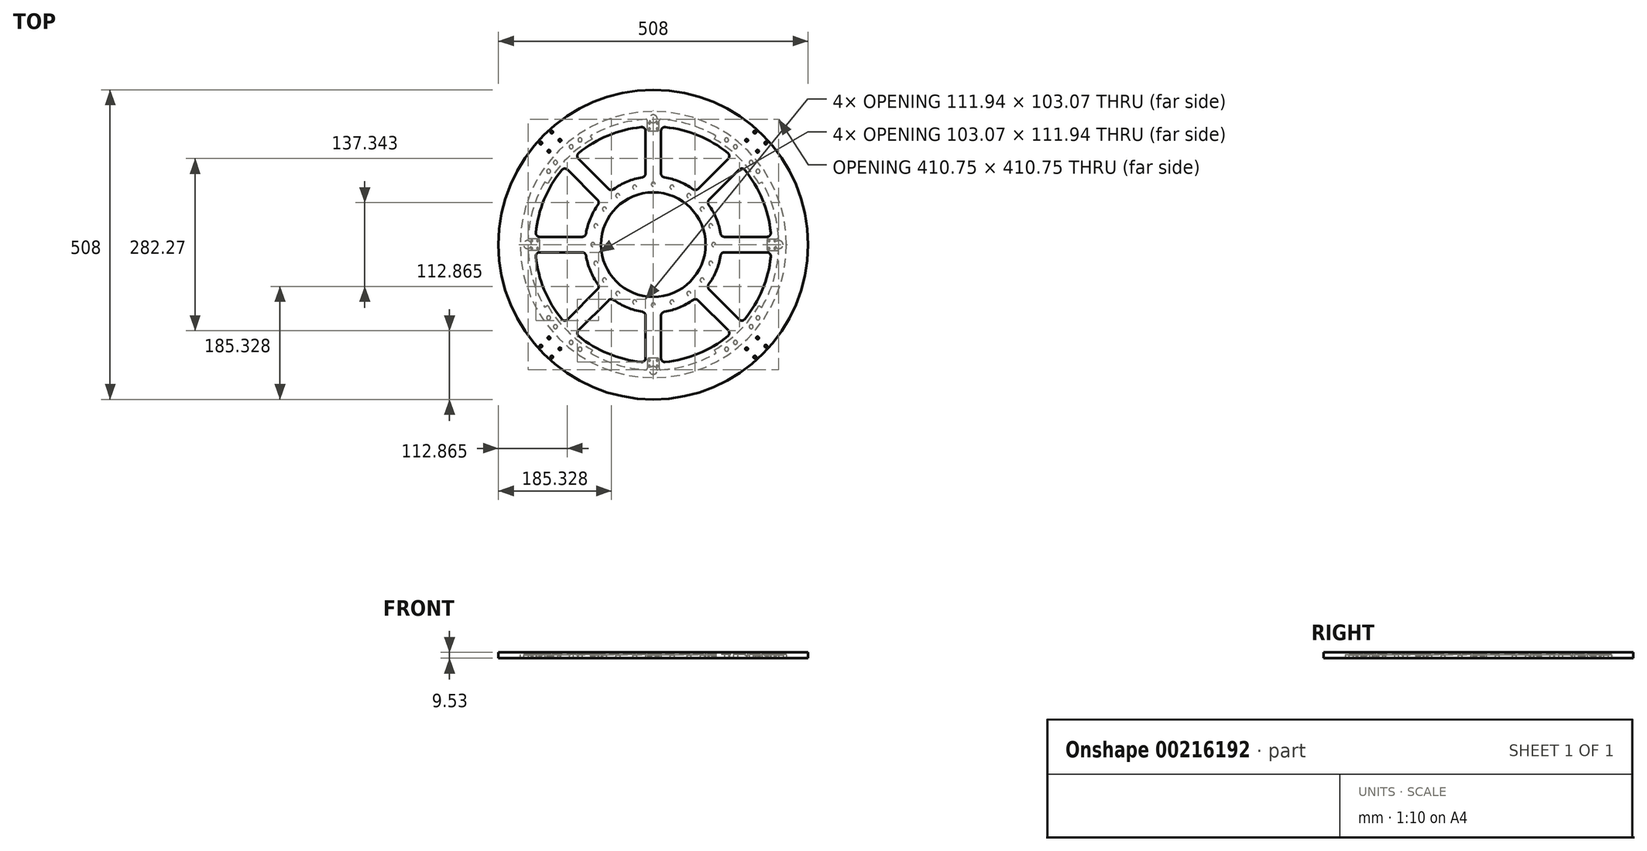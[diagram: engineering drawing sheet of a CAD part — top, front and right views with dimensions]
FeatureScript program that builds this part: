
annotation { "Feature Type Name" : "Feature", "Feature Type Description" : "" }
export const myFeature = defineFeature(function(context is Context, id is Id, definition is map)
    precondition{}
    {
        {
            var Q0;
            Q0=qCreatedBy(makeId("Top.planeOp"),FACE);
            var sketch = newSketch(context, id + "F0", { "sketchPlane" : qUnion([Q0])});
            skCircle(sketch, "E0", {"center": v(0, 0) * mm, "radius": 218.44 * mm});
            skArc(sketch, "E1", {"start": v(205.38, 12.22) * mm, "mid": v(197.06, 59.13) * mm, "end": v(178.18, 102.87) * mm});
            skLineSegment(sketch, "E2", {"start": v(0, 0) * mm, "end": v(218.44, 0) * mm});
            skLineSegment(sketch, "E3", {"start": v(199.4, 6.35) * mm, "end": v(189.87, 6.35) * mm});
            skLineSegment(sketch, "E4.MirrorCS", {"start": v(199.4, -6.35) * mm, "end": v(189.87, -6.35) * mm});
            skLineSegment(sketch, "E5.bottom", {"start": v(188.91, 9.52) * mm, "end": v(202.88, 9.52) * mm});
            skLineSegment(sketch, "E5.top", {"start": v(188.91, -9.52) * mm, "end": v(202.88, -9.52) * mm});
            skLineSegment(sketch, "E5.left", {"start": v(186.37, 6.98) * mm, "end": v(186.37, -6.98) * mm});
            skPoint(sketch, "E5.middle", {"position": v(194.63, 0) * mm});
            skLineSegment(sketch, "E6", {"start": v(202.84, 9.52) * mm, "end": v(202.88, 9.52) * mm});
            skPoint(sketch, "E7.orphan", {"position": v(199.4, -6.35) * mm});
            skPoint(sketch, "E8.orphan", {"position": v(205.74, 12.7) * mm});
            skPoint(sketch, "E9.start.orphan", {"position": v(205.74, 0) * mm});
            skPoint(sketch, "E10.visualSharp", {"position": v(205.52, 9.52) * mm});
            skArc(sketch, "E10.filletArc", {"start": v(202.84, 9.52) * mm, "mid": v(204.7, 10.32) * mm, "end": v(205.38, 12.22) * mm});
            skPoint(sketch, "E11.orphan", {"position": v(205.74, -12.7) * mm});
            skPoint(sketch, "E12.MirrorCS.end.orphan", {"position": v(205.74, -6.35) * mm});
            skLineSegment(sketch, "E13", {"start": v(202.84, -9.52) * mm, "end": v(202.88, -9.52) * mm});
            skArc(sketch, "E14.filletArc", {"start": v(205.38, -12.22) * mm, "mid": v(204.7, -10.32) * mm, "end": v(202.84, -9.52) * mm});
            skPoint(sketch, "E15.visualSharp", {"position": v(186.37, 9.52) * mm});
            skArc(sketch, "E15.filletArc", {"start": v(188.91, 9.52) * mm, "mid": v(187.12, 8.78) * mm, "end": v(186.37, 6.98) * mm});
            skPoint(sketch, "E16.visualSharp", {"position": v(186.37, -9.53) * mm});
            skArc(sketch, "E16.filletArc", {"start": v(186.37, -6.98) * mm, "mid": v(187.12, -8.78) * mm, "end": v(188.91, -9.52) * mm});
            skPoint(sketch, "E17.start.orphan", {"position": v(205.74, 6.35) * mm});
            skPoint(sketch, "E18.1.0", {"position": v(-6.35, 205.74) * mm});
            skPoint(sketch, "E18.1.1", {"position": v(-12.7, 205.74) * mm});
            skPoint(sketch, "E18.1.2", {"position": v(6.35, 205.74) * mm});
            skPoint(sketch, "E18.1.3", {"position": v(6.35, 199.4) * mm});
            skPoint(sketch, "E18.1.4", {"position": v(12.7, 205.74) * mm});
            skPoint(sketch, "E18.1.5", {"position": v(9.53, 186.37) * mm});
            skPoint(sketch, "E18.1.6", {"position": v(-9.52, 186.37) * mm});
            skPoint(sketch, "E18.1.7", {"position": v(0, 194.63) * mm});
            skPoint(sketch, "E18.1.8", {"position": v(6.35, 205.74) * mm});
            skPoint(sketch, "E18.1.9", {"position": v(-9.52, 205.52) * mm});
            skPoint(sketch, "E18.1.10", {"position": v(0, 205.74) * mm});
            skLineSegment(sketch, "E18.1.11", {"start": v(-6.98, 186.37) * mm, "end": v(6.99, 186.37) * mm});
            skPoint(sketch, "E18.1.12", {"position": v(0, 205.74) * mm});
            skLineSegment(sketch, "E18.1.13", {"start": v(9.53, 188.91) * mm, "end": v(9.53, 202.88) * mm});
            skLineSegment(sketch, "E18.1.14", {"start": v(-9.52, 188.91) * mm, "end": v(-9.52, 202.88) * mm});
            skLineSegment(sketch, "E18.1.15", {"start": v(6.35, 199.4) * mm, "end": v(6.35, 189.87) * mm});
            skLineSegment(sketch, "E18.1.16", {"start": v(-6.35, 199.4) * mm, "end": v(-6.35, 189.87) * mm});
            skArc(sketch, "E18.1.17", {"start": v(-9.52, 188.91) * mm, "mid": v(-8.78, 187.12) * mm, "end": v(-6.98, 186.37) * mm});
            skPoint(sketch, "E18.1.18", {"position": v(0, 205.74) * mm});
            skArc(sketch, "E18.1.19", {"start": v(6.99, 186.37) * mm, "mid": v(8.78, 187.12) * mm, "end": v(9.53, 188.91) * mm});
            skArc(sketch, "E18.1.20", {"start": v(12.22, 205.38) * mm, "mid": v(10.32, 204.7) * mm, "end": v(9.53, 202.84) * mm});
            skArc(sketch, "E18.1.21", {"start": v(-9.52, 202.84) * mm, "mid": v(-10.32, 204.7) * mm, "end": v(-12.22, 205.38) * mm});
            skLineSegment(sketch, "E18.1.22", {"start": v(-9.52, 202.84) * mm, "end": v(-9.52, 202.88) * mm});
            skLineSegment(sketch, "E18.1.23", {"start": v(9.53, 202.84) * mm, "end": v(9.53, 202.88) * mm});
            skPoint(sketch, "E18.2.0", {"position": v(-205.74, -6.35) * mm});
            skPoint(sketch, "E18.2.1", {"position": v(-205.74, -12.7) * mm});
            skPoint(sketch, "E18.2.2", {"position": v(-205.74, 6.35) * mm});
            skPoint(sketch, "E18.2.3", {"position": v(-199.4, 6.35) * mm});
            skPoint(sketch, "E18.2.4", {"position": v(-205.74, 12.7) * mm});
            skPoint(sketch, "E18.2.5", {"position": v(-186.37, 9.53) * mm});
            skPoint(sketch, "E18.2.6", {"position": v(-186.37, -9.52) * mm});
            skPoint(sketch, "E18.2.7", {"position": v(-194.63, 0) * mm});
            skPoint(sketch, "E18.2.8", {"position": v(-205.74, 6.35) * mm});
            skPoint(sketch, "E18.2.9", {"position": v(-205.52, -9.52) * mm});
            skPoint(sketch, "E18.2.10", {"position": v(-205.74, 0) * mm});
            skLineSegment(sketch, "E18.2.11", {"start": v(-186.37, -6.98) * mm, "end": v(-186.37, 6.99) * mm});
            skPoint(sketch, "E18.2.12", {"position": v(-205.74, 0) * mm});
            skLineSegment(sketch, "E18.2.13", {"start": v(-188.91, 9.53) * mm, "end": v(-202.88, 9.53) * mm});
            skLineSegment(sketch, "E18.2.14", {"start": v(-188.91, -9.52) * mm, "end": v(-202.88, -9.52) * mm});
            skLineSegment(sketch, "E18.2.15", {"start": v(-199.4, 6.35) * mm, "end": v(-189.87, 6.35) * mm});
            skLineSegment(sketch, "E18.2.16", {"start": v(-199.4, -6.35) * mm, "end": v(-189.87, -6.35) * mm});
            skArc(sketch, "E18.2.17", {"start": v(-188.91, -9.52) * mm, "mid": v(-187.12, -8.78) * mm, "end": v(-186.37, -6.98) * mm});
            skPoint(sketch, "E18.2.18", {"position": v(-205.74, 0) * mm});
            skArc(sketch, "E18.2.19", {"start": v(-186.37, 6.99) * mm, "mid": v(-187.12, 8.78) * mm, "end": v(-188.91, 9.53) * mm});
            skArc(sketch, "E18.2.20", {"start": v(-205.38, 12.22) * mm, "mid": v(-204.7, 10.32) * mm, "end": v(-202.84, 9.53) * mm});
            skArc(sketch, "E18.2.21", {"start": v(-202.84, -9.52) * mm, "mid": v(-204.7, -10.32) * mm, "end": v(-205.38, -12.22) * mm});
            skLineSegment(sketch, "E18.2.22", {"start": v(-202.84, -9.52) * mm, "end": v(-202.88, -9.52) * mm});
            skLineSegment(sketch, "E18.2.23", {"start": v(-202.84, 9.53) * mm, "end": v(-202.88, 9.53) * mm});
            skPoint(sketch, "E18.3.0", {"position": v(6.35, -205.74) * mm});
            skPoint(sketch, "E18.3.1", {"position": v(12.7, -205.74) * mm});
            skPoint(sketch, "E18.3.2", {"position": v(-6.35, -205.74) * mm});
            skPoint(sketch, "E18.3.3", {"position": v(-6.35, -199.4) * mm});
            skPoint(sketch, "E18.3.4", {"position": v(-12.7, -205.74) * mm});
            skPoint(sketch, "E18.3.5", {"position": v(-9.53, -186.37) * mm});
            skPoint(sketch, "E18.3.6", {"position": v(9.52, -186.37) * mm});
            skPoint(sketch, "E18.3.7", {"position": v(0, -194.63) * mm});
            skPoint(sketch, "E18.3.8", {"position": v(-6.35, -205.74) * mm});
            skPoint(sketch, "E18.3.9", {"position": v(9.52, -205.52) * mm});
            skPoint(sketch, "E18.3.10", {"position": v(0, -205.74) * mm});
            skLineSegment(sketch, "E18.3.11", {"start": v(6.98, -186.37) * mm, "end": v(-6.99, -186.37) * mm});
            skPoint(sketch, "E18.3.12", {"position": v(0, -205.74) * mm});
            skLineSegment(sketch, "E18.3.13", {"start": v(-9.53, -188.91) * mm, "end": v(-9.53, -202.88) * mm});
            skLineSegment(sketch, "E18.3.14", {"start": v(9.52, -188.91) * mm, "end": v(9.52, -202.88) * mm});
            skLineSegment(sketch, "E18.3.15", {"start": v(-6.35, -199.4) * mm, "end": v(-6.35, -189.87) * mm});
            skLineSegment(sketch, "E18.3.16", {"start": v(6.35, -199.4) * mm, "end": v(6.35, -189.87) * mm});
            skArc(sketch, "E18.3.17", {"start": v(9.52, -188.91) * mm, "mid": v(8.78, -187.12) * mm, "end": v(6.98, -186.37) * mm});
            skPoint(sketch, "E18.3.18", {"position": v(0, -205.74) * mm});
            skArc(sketch, "E18.3.19", {"start": v(-6.99, -186.37) * mm, "mid": v(-8.78, -187.12) * mm, "end": v(-9.53, -188.91) * mm});
            skArc(sketch, "E18.3.20", {"start": v(-12.22, -205.38) * mm, "mid": v(-10.32, -204.7) * mm, "end": v(-9.53, -202.84) * mm});
            skArc(sketch, "E18.3.21", {"start": v(9.52, -202.84) * mm, "mid": v(10.32, -204.7) * mm, "end": v(12.22, -205.38) * mm});
            skLineSegment(sketch, "E18.3.22", {"start": v(9.53, -202.84) * mm, "end": v(9.53, -202.88) * mm});
            skLineSegment(sketch, "E18.3.23", {"start": v(-9.53, -202.84) * mm, "end": v(-9.53, -202.88) * mm});
            skArc(sketch, "E19.trimOffspring", {"start": v(-12.22, 205.38) * mm, "mid": v(-59.13, 197.06) * mm, "end": v(-102.87, 178.18) * mm});
            skArc(sketch, "E20.trimOffspring", {"start": v(-205.38, -12.22) * mm, "mid": v(-197.06, -59.13) * mm, "end": v(-178.18, -102.87) * mm});
            skArc(sketch, "E21.trimOffspring", {"start": v(12.22, -205.38) * mm, "mid": v(59.13, -197.06) * mm, "end": v(102.87, -178.18) * mm});
            skLineSegment(sketch, "E22", {"start": v(0, 0) * mm, "end": v(154.46, 154.46) * mm});
            skLineSegment(sketch, "E23", {"start": v(173.23, 100.01) * mm, "end": v(178.18, 102.87) * mm});
            skLineSegment(sketch, "E24.MirrorCS", {"start": v(100.01, 173.23) * mm, "end": v(102.87, 178.18) * mm});
            skArc(sketch, "E25.trimOffspring", {"start": v(173.23, 100.01) * mm, "mid": v(141.44, 141.44) * mm, "end": v(100.01, 173.23) * mm});
            skPoint(sketch, "E26.orphan", {"position": v(109.22, 189.17) * mm});
            skPoint(sketch, "E27.orphan", {"position": v(189.17, 109.22) * mm});
            skArc(sketch, "E28.1.0", {"start": v(-100.01, 173.23) * mm, "mid": v(-141.44, 141.44) * mm, "end": v(-173.23, 100.01) * mm});
            skLineSegment(sketch, "E28.1.1", {"start": v(-173.23, 100.01) * mm, "end": v(-178.18, 102.87) * mm});
            skLineSegment(sketch, "E28.1.2", {"start": v(-100.01, 173.23) * mm, "end": v(-102.87, 178.18) * mm});
            skArc(sketch, "E28.2.0", {"start": v(-173.23, -100.01) * mm, "mid": v(-141.44, -141.44) * mm, "end": v(-100.01, -173.23) * mm});
            skLineSegment(sketch, "E28.2.1", {"start": v(-100.01, -173.23) * mm, "end": v(-102.87, -178.18) * mm});
            skLineSegment(sketch, "E28.2.2", {"start": v(-173.23, -100.01) * mm, "end": v(-178.18, -102.87) * mm});
            skArc(sketch, "E28.3.0", {"start": v(100.01, -173.23) * mm, "mid": v(141.44, -141.44) * mm, "end": v(173.23, -100.01) * mm});
            skLineSegment(sketch, "E28.3.1", {"start": v(173.23, -100.01) * mm, "end": v(178.18, -102.87) * mm});
            skLineSegment(sketch, "E28.3.2", {"start": v(100.01, -173.23) * mm, "end": v(102.87, -178.18) * mm});
            skArc(sketch, "E29.trimOffspring", {"start": v(-178.18, 102.87) * mm, "mid": v(-197.06, 59.13) * mm, "end": v(-205.38, 12.22) * mm});
            skArc(sketch, "E30.trimOffspring", {"start": v(-102.87, -178.18) * mm, "mid": v(-59.13, -197.06) * mm, "end": v(-12.22, -205.38) * mm});
            skArc(sketch, "E31.trimOffspring", {"start": v(178.18, -102.87) * mm, "mid": v(197.06, -59.13) * mm, "end": v(205.38, -12.22) * mm});
            skArc(sketch, "E32.trimOffspring", {"start": v(102.87, 178.18) * mm, "mid": v(59.13, 197.06) * mm, "end": v(12.22, 205.38) * mm});
            skArc(sketch, "E33", {"start": v(209.55, 0) * mm, "mid": v(185.87, 96.76) * mm, "end": v(120.2, 171.65) * mm});
            skLineSegment(sketch, "E34", {"start": v(128.57, 153.23) * mm, "end": v(134.7, 160.52) * mm});
            skLineSegment(sketch, "E35", {"start": v(114.73, 163.85) * mm, "end": v(120.2, 171.65) * mm});
            skLineSegment(sketch, "E36.MirrorCS", {"start": v(153.23, 128.57) * mm, "end": v(160.52, 134.7) * mm});
            skLineSegment(sketch, "E37.MirrorCS", {"start": v(163.85, 114.73) * mm, "end": v(171.65, 120.2) * mm});
            skPoint(sketch, "E38.orphan", {"position": v(125.3, 178.94) * mm});
            skPoint(sketch, "E39.orphan", {"position": v(140.41, 167.33) * mm});
            skPoint(sketch, "E40.orphan", {"position": v(167.33, 140.41) * mm});
            skPoint(sketch, "E41.orphan", {"position": v(178.94, 125.3) * mm});
            skLineSegment(sketch, "E42.1.0", {"start": v(-163.85, 114.73) * mm, "end": v(-171.65, 120.2) * mm});
            skLineSegment(sketch, "E42.1.1", {"start": v(-153.23, 128.57) * mm, "end": v(-160.52, 134.7) * mm});
            skLineSegment(sketch, "E42.1.2", {"start": v(-128.57, 153.23) * mm, "end": v(-134.7, 160.52) * mm});
            skLineSegment(sketch, "E42.1.3", {"start": v(-114.73, 163.85) * mm, "end": v(-120.2, 171.65) * mm});
            skLineSegment(sketch, "E42.2.0", {"start": v(-114.73, -163.85) * mm, "end": v(-120.2, -171.65) * mm});
            skLineSegment(sketch, "E42.2.1", {"start": v(-128.57, -153.23) * mm, "end": v(-134.7, -160.52) * mm});
            skLineSegment(sketch, "E42.2.2", {"start": v(-153.23, -128.57) * mm, "end": v(-160.52, -134.7) * mm});
            skLineSegment(sketch, "E42.2.3", {"start": v(-163.85, -114.73) * mm, "end": v(-171.65, -120.2) * mm});
            skLineSegment(sketch, "E42.3.0", {"start": v(163.85, -114.73) * mm, "end": v(171.65, -120.2) * mm});
            skLineSegment(sketch, "E42.3.1", {"start": v(153.23, -128.57) * mm, "end": v(160.52, -134.7) * mm});
            skLineSegment(sketch, "E42.3.2", {"start": v(128.57, -153.23) * mm, "end": v(134.7, -160.52) * mm});
            skLineSegment(sketch, "E42.3.3", {"start": v(114.73, -163.85) * mm, "end": v(120.2, -171.65) * mm});
            skLineSegment(sketch, "E43", {"start": v(205.74, 0) * mm, "end": v(205.74, -4.72) * mm});
            skLineSegment(sketch, "E44", {"start": v(199.4, -6.35) * mm, "end": v(199.4, 0) * mm});
            skSolve(sketch);
        }
        {
            var Q0;
            Q0 = qSketchRegion(id + "F0", true);
            var Q1;
            Q1=makeQuery(id+"F0.imprint","IMPRINT",FACE,{"disambiguationData":[TD([[makeQuery(id+"F0.imprint","IMPRINT",EDGE,{"derivedFrom":sQuery(id+"F0.wireOp",EDGE,"E1")}),-1.0]])]});
            var Q2;
            {var subQ0=sQuery(id+"F0.wireOp",EDGE,"E36.MirrorCS");Q2=makeQuery(id+"F0.imprint","IMPRINT",FACE,{"disambiguationData":[TD([[makeQuery(id+"F0.imprint","IMPRINT",EDGE,{"derivedFrom":subQ0}),-1.0]])]});}
            var Q3;
            {var subQ5=sQuery(id+"F0.wireOp",EDGE,"E36.MirrorCS");Q3=makeQuery(id+"F0.imprint","IMPRINT",FACE,{"disambiguationData":[TD([[makeQuery(id+"F0.imprint","IMPRINT",EDGE,{"derivedFrom":subQ5}),1.0]])]});}
            var Q4;
            {var subQ5=sQuery(id+"F0.wireOp",EDGE,"E34");Q4=makeQuery(id+"F0.imprint","IMPRINT",FACE,{"disambiguationData":[TD([[makeQuery(id+"F0.imprint","IMPRINT",EDGE,{"derivedFrom":subQ5}),-1.0]])]});}
            var Q5;
            {var subQ0=sQuery(id+"F0.wireOp",EDGE,"E34");Q5=makeQuery(id+"F0.imprint","IMPRINT",FACE,{"disambiguationData":[TD([[makeQuery(id+"F0.imprint","IMPRINT",EDGE,{"derivedFrom":subQ0}),1.0]])]});}
            extrude(context, id + "F1", {"entities" : qUnion([Q0, Q1, Q2, Q3, Q4, Q5]), "depth" : 6.1 * mm});
        }
        {
            var Q0;
            Q0=sQuery(id+"F0.wireOp",VERTEX,"E42.1.0.end");
            var Q1;
            Q1=sQuery(id+"F0.wireOp",VERTEX,"E42.1.1.end");
            var Q2;
            Q2=sQuery(id+"F0.wireOp",VERTEX,"E42.1.2.end");
            var Q3;
            Q3=sQuery(id+"F0.wireOp",VERTEX,"E42.1.3.end");
            var Q4;
            Q4=sQuery(id+"F0.wireOp",VERTEX,"E35.end");
            var Q5;
            Q5=sQuery(id+"F0.wireOp",VERTEX,"E34.end");
            var Q6;
            Q6=sQuery(id+"F0.wireOp",VERTEX,"E36.MirrorCS.end");
            var Q7;
            Q7=sQuery(id+"F0.wireOp",VERTEX,"E37.MirrorCS.end");
            var Q8;
            Q8=sQuery(id+"F0.wireOp",VERTEX,"E42.3.0.end");
            var Q9;
            Q9=sQuery(id+"F0.wireOp",VERTEX,"E42.3.1.end");
            var Q10;
            Q10=sQuery(id+"F0.wireOp",VERTEX,"E42.3.2.end");
            var Q11;
            Q11=sQuery(id+"F0.wireOp",VERTEX,"E42.3.3.end");
            var Q12;
            Q12=sQuery(id+"F0.wireOp",VERTEX,"E42.2.0.end");
            var Q13;
            Q13=sQuery(id+"F0.wireOp",VERTEX,"E42.2.1.end");
            var Q14;
            Q14=sQuery(id+"F0.wireOp",VERTEX,"E42.2.2.end");
            var Q15;
            Q15=sQuery(id+"F0.wireOp",VERTEX,"E42.2.3.end");
            var Q16;
            Q16=makeQuery(id+"F1.opExtrude","SWEPT_BODY",BODY,{"disambiguationData":[OSD([sQuery(id+"F0.wireOp",EDGE,"E0"),sQuery(id+"F0.wireOp",EDGE,"E1"),sQuery(id+"F0.wireOp",EDGE,"E5.bottom"),sQuery(id+"F0.wireOp",EDGE,"E5.top"),sQuery(id+"F0.wireOp",EDGE,"E5.left"),sQuery(id+"F0.wireOp",EDGE,"E10.filletArc"),sQuery(id+"F0.wireOp",EDGE,"E14.filletArc"),sQuery(id+"F0.wireOp",EDGE,"E15.filletArc"),sQuery(id+"F0.wireOp",EDGE,"E16.filletArc"),sQuery(id+"F0.wireOp",EDGE,"E18.1.11"),sQuery(id+"F0.wireOp",EDGE,"E18.1.13"),sQuery(id+"F0.wireOp",EDGE,"E18.1.14"),sQuery(id+"F0.wireOp",EDGE,"E18.1.17"),sQuery(id+"F0.wireOp",EDGE,"E18.1.19"),sQuery(id+"F0.wireOp",EDGE,"E18.1.20"),sQuery(id+"F0.wireOp",EDGE,"E18.1.21"),sQuery(id+"F0.wireOp",EDGE,"E18.2.11"),sQuery(id+"F0.wireOp",EDGE,"E18.2.13"),sQuery(id+"F0.wireOp",EDGE,"E18.2.14"),sQuery(id+"F0.wireOp",EDGE,"E18.2.17"),sQuery(id+"F0.wireOp",EDGE,"E18.2.19"),sQuery(id+"F0.wireOp",EDGE,"E18.2.20"),sQuery(id+"F0.wireOp",EDGE,"E18.2.21"),sQuery(id+"F0.wireOp",EDGE,"E18.3.11"),sQuery(id+"F0.wireOp",EDGE,"E18.3.13"),sQuery(id+"F0.wireOp",EDGE,"E18.3.14"),sQuery(id+"F0.wireOp",EDGE,"E18.3.17"),sQuery(id+"F0.wireOp",EDGE,"E18.3.19"),sQuery(id+"F0.wireOp",EDGE,"E18.3.20"),sQuery(id+"F0.wireOp",EDGE,"E18.3.21"),sQuery(id+"F0.wireOp",EDGE,"E19.trimOffspring"),sQuery(id+"F0.wireOp",EDGE,"E20.trimOffspring"),sQuery(id+"F0.wireOp",EDGE,"E21.trimOffspring"),sQuery(id+"F0.wireOp",EDGE,"E23"),sQuery(id+"F0.wireOp",EDGE,"E24.MirrorCS"),sQuery(id+"F0.wireOp",EDGE,"E25.trimOffspring"),sQuery(id+"F0.wireOp",EDGE,"E28.1.0"),sQuery(id+"F0.wireOp",EDGE,"E28.1.1"),sQuery(id+"F0.wireOp",EDGE,"E28.1.2"),sQuery(id+"F0.wireOp",EDGE,"E28.2.0"),sQuery(id+"F0.wireOp",EDGE,"E28.2.1"),sQuery(id+"F0.wireOp",EDGE,"E28.2.2"),sQuery(id+"F0.wireOp",EDGE,"E28.3.0"),sQuery(id+"F0.wireOp",EDGE,"E28.3.1"),sQuery(id+"F0.wireOp",EDGE,"E28.3.2"),sQuery(id+"F0.wireOp",EDGE,"E29.trimOffspring"),sQuery(id+"F0.wireOp",EDGE,"E30.trimOffspring"),sQuery(id+"F0.wireOp",EDGE,"E31.trimOffspring"),sQuery(id+"F0.wireOp",EDGE,"E32.trimOffspring")])]});
            hole(context, id + "F2", {"style" : HoleStyle.SIMPLE, "endStyle" : HoleEndStyle.BLIND, "oppositeDirection" : true, "standardTappedOrClearance" : lookupTablePath({ "standard" : "ANSI", "fit" : "Close", "size" : "1/4", "type" : "Clearance" }), "standardBlindInLast" : lookupTablePath({ "fit" : "Close", "standard" : "ANSI", "size" : "1/4", "type" : "Clearance" }), "holeDiameter" : 6.53 * mm, "holeDepth" : 7.62 * mm, "locations" : qUnion([Q0, Q1, Q2, Q3, Q4, Q5, Q6, Q7, Q8, Q9, Q10, Q11, Q12, Q13, Q14, Q15]), "scope" : qUnion([Q16])});
        }
        {
            var Q0;
            Q0=sQuery(id+"F0.wireOp",VERTEX,"E18.1.16.start");
            var Q1;
            Q1=sQuery(id+"F0.wireOp",VERTEX,"E18.1.16.end");
            var Q2;
            Q2=sQuery(id+"F0.wireOp",VERTEX,"E18.1.3");
            var Q3;
            Q3=sQuery(id+"F0.wireOp",VERTEX,"E18.1.15.end");
            var Q4;
            Q4=sQuery(id+"F0.wireOp",VERTEX,"E3.end");
            var Q5;
            Q5=sQuery(id+"F0.wireOp",VERTEX,"E4.MirrorCS.end");
            var Q6;
            Q6=sQuery(id+"F0.wireOp",VERTEX,"E7.orphan");
            var Q7;
            Q7=sQuery(id+"F0.wireOp",VERTEX,"E3.start");
            var Q8;
            Q8=sQuery(id+"F0.wireOp",VERTEX,"E18.2.16.start");
            var Q9;
            Q9=sQuery(id+"F0.wireOp",VERTEX,"E18.2.3");
            var Q10;
            Q10=sQuery(id+"F0.wireOp",VERTEX,"E18.2.15.end");
            var Q11;
            Q11=sQuery(id+"F0.wireOp",VERTEX,"E18.2.16.end");
            var Q12;
            Q12=sQuery(id+"F0.wireOp",VERTEX,"E18.3.16.start");
            var Q13;
            Q13=sQuery(id+"F0.wireOp",VERTEX,"E18.3.16.end");
            var Q14;
            Q14=sQuery(id+"F0.wireOp",VERTEX,"E18.3.15.end");
            var Q15;
            Q15=sQuery(id+"F0.wireOp",VERTEX,"E18.3.3");
            var Q16;
            Q16=makeQuery(id+"F1.opExtrude","SWEPT_BODY",BODY,{"disambiguationData":[OSD([sQuery(id+"F0.wireOp",EDGE,"E0"),sQuery(id+"F0.wireOp",EDGE,"E1"),sQuery(id+"F0.wireOp",EDGE,"E5.bottom"),sQuery(id+"F0.wireOp",EDGE,"E5.top"),sQuery(id+"F0.wireOp",EDGE,"E5.left"),sQuery(id+"F0.wireOp",EDGE,"E10.filletArc"),sQuery(id+"F0.wireOp",EDGE,"E14.filletArc"),sQuery(id+"F0.wireOp",EDGE,"E15.filletArc"),sQuery(id+"F0.wireOp",EDGE,"E16.filletArc"),sQuery(id+"F0.wireOp",EDGE,"E18.1.11"),sQuery(id+"F0.wireOp",EDGE,"E18.1.13"),sQuery(id+"F0.wireOp",EDGE,"E18.1.14"),sQuery(id+"F0.wireOp",EDGE,"E18.1.17"),sQuery(id+"F0.wireOp",EDGE,"E18.1.19"),sQuery(id+"F0.wireOp",EDGE,"E18.1.20"),sQuery(id+"F0.wireOp",EDGE,"E18.1.21"),sQuery(id+"F0.wireOp",EDGE,"E18.2.11"),sQuery(id+"F0.wireOp",EDGE,"E18.2.13"),sQuery(id+"F0.wireOp",EDGE,"E18.2.14"),sQuery(id+"F0.wireOp",EDGE,"E18.2.17"),sQuery(id+"F0.wireOp",EDGE,"E18.2.19"),sQuery(id+"F0.wireOp",EDGE,"E18.2.20"),sQuery(id+"F0.wireOp",EDGE,"E18.2.21"),sQuery(id+"F0.wireOp",EDGE,"E18.3.11"),sQuery(id+"F0.wireOp",EDGE,"E18.3.13"),sQuery(id+"F0.wireOp",EDGE,"E18.3.14"),sQuery(id+"F0.wireOp",EDGE,"E18.3.17"),sQuery(id+"F0.wireOp",EDGE,"E18.3.19"),sQuery(id+"F0.wireOp",EDGE,"E18.3.20"),sQuery(id+"F0.wireOp",EDGE,"E18.3.21"),sQuery(id+"F0.wireOp",EDGE,"E19.trimOffspring"),sQuery(id+"F0.wireOp",EDGE,"E20.trimOffspring"),sQuery(id+"F0.wireOp",EDGE,"E21.trimOffspring"),sQuery(id+"F0.wireOp",EDGE,"E23"),sQuery(id+"F0.wireOp",EDGE,"E24.MirrorCS"),sQuery(id+"F0.wireOp",EDGE,"E25.trimOffspring"),sQuery(id+"F0.wireOp",EDGE,"E28.1.0"),sQuery(id+"F0.wireOp",EDGE,"E28.1.1"),sQuery(id+"F0.wireOp",EDGE,"E28.1.2"),sQuery(id+"F0.wireOp",EDGE,"E28.2.0"),sQuery(id+"F0.wireOp",EDGE,"E28.2.1"),sQuery(id+"F0.wireOp",EDGE,"E28.2.2"),sQuery(id+"F0.wireOp",EDGE,"E28.3.0"),sQuery(id+"F0.wireOp",EDGE,"E28.3.1"),sQuery(id+"F0.wireOp",EDGE,"E28.3.2"),sQuery(id+"F0.wireOp",EDGE,"E29.trimOffspring"),sQuery(id+"F0.wireOp",EDGE,"E30.trimOffspring"),sQuery(id+"F0.wireOp",EDGE,"E31.trimOffspring"),sQuery(id+"F0.wireOp",EDGE,"E32.trimOffspring")])]});
            hole(context, id + "F3", {"style" : HoleStyle.SIMPLE, "endStyle" : HoleEndStyle.BLIND, "oppositeDirection" : true, "standardTappedOrClearance" : lookupTablePath({ "standard" : "ANSI", "fit" : "Close", "size" : "#4", "type" : "Clearance" }), "standardBlindInLast" : lookupTablePath({ "fit" : "Close", "standard" : "ANSI", "size" : "#4", "type" : "Clearance" }), "holeDiameter" : 2.95 * mm, "holeDepth" : 7.62 * mm, "locations" : qUnion([Q0, Q1, Q2, Q3, Q4, Q5, Q6, Q7, Q8, Q9, Q10, Q11, Q12, Q13, Q14, Q15]), "scope" : qUnion([Q16])});
        }
        {
            var Q0;
            Q0=qCreatedBy(makeId("Top.planeOp"),FACE);
            var sketch = newSketch(context, id + "F4", { "sketchPlane" : qUnion([Q0])});
            skCircle(sketch, "E45", {"center": v(0, 0) * mm, "radius": 206.38 * mm});
            skCircle(sketch, "E46", {"center": v(0, 0) * mm, "radius": 254 * mm});
            skCircle(sketch, "E47", {"center": v(0, 0) * mm, "radius": 99.1 * mm});
            skLineSegment(sketch, "E48", {"start": v(0, 0) * mm, "end": v(0, 99.1) * mm});
            skLineSegment(sketch, "E49", {"start": v(0, 0) * mm, "end": v(30.63, 94.26) * mm});
            skLineSegment(sketch, "E50", {"start": v(0, 0) * mm, "end": v(58.25, 80.18) * mm});
            skLineSegment(sketch, "E51", {"start": v(0, 0) * mm, "end": v(80.18, 58.25) * mm});
            skLineSegment(sketch, "E52", {"start": v(0, 0) * mm, "end": v(94.26, 30.63) * mm});
            skLineSegment(sketch, "E53.1.0", {"start": v(0, 0) * mm, "end": v(-99.1, 0) * mm});
            skLineSegment(sketch, "E53.1.1", {"start": v(0, 0) * mm, "end": v(-94.26, 30.63) * mm});
            skLineSegment(sketch, "E53.1.2", {"start": v(0, 0) * mm, "end": v(-80.18, 58.25) * mm});
            skLineSegment(sketch, "E53.1.3", {"start": v(0, 0) * mm, "end": v(-58.25, 80.18) * mm});
            skLineSegment(sketch, "E53.1.4", {"start": v(0, 0) * mm, "end": v(-30.63, 94.26) * mm});
            skLineSegment(sketch, "E53.2.0", {"start": v(0, 0) * mm, "end": v(0, -99.1) * mm});
            skLineSegment(sketch, "E53.2.1", {"start": v(0, 0) * mm, "end": v(-30.63, -94.26) * mm});
            skLineSegment(sketch, "E53.2.2", {"start": v(0, 0) * mm, "end": v(-58.25, -80.18) * mm});
            skLineSegment(sketch, "E53.2.3", {"start": v(0, 0) * mm, "end": v(-80.18, -58.25) * mm});
            skLineSegment(sketch, "E53.2.4", {"start": v(0, 0) * mm, "end": v(-94.26, -30.63) * mm});
            skLineSegment(sketch, "E53.3.0", {"start": v(0, 0) * mm, "end": v(99.1, 0) * mm});
            skLineSegment(sketch, "E53.3.1", {"start": v(0, 0) * mm, "end": v(94.26, -30.63) * mm});
            skLineSegment(sketch, "E53.3.2", {"start": v(0, 0) * mm, "end": v(80.18, -58.25) * mm});
            skLineSegment(sketch, "E53.3.3", {"start": v(0, 0) * mm, "end": v(58.25, -80.18) * mm});
            skLineSegment(sketch, "E53.3.4", {"start": v(0, 0) * mm, "end": v(30.63, -94.26) * mm});
            skLineSegment(sketch, "E54", {"start": v(0, 99.1) * mm, "end": v(0, 206.38) * mm});
            skLineSegment(sketch, "E55", {"start": v(70.08, 70.08) * mm, "end": v(145.93, 145.93) * mm});
            skArc(sketch, "E56.0", {"start": v(122.31, 150.17) * mm, "mid": v(74.12, 178.93) * mm, "end": v(19.7, 192.67) * mm});
            skLineSegment(sketch, "E57.0", {"start": v(12.7, 116.61) * mm, "end": v(12.7, 186.35) * mm});
            skLineSegment(sketch, "E58.0", {"start": v(73.48, 91.44) * mm, "end": v(122.8, 140.75) * mm});
            skArc(sketch, "E59.0", {"start": v(65.28, 90.77) * mm, "mid": v(42.79, 103.3) * mm, "end": v(18.03, 110.35) * mm});
            skLineSegment(sketch, "E60.trimOffspring", {"start": v(12.7, 205.98) * mm, "end": v(12.7, 206.38) * mm});
            skLineSegment(sketch, "E61.trimOffspring", {"start": v(136.67, 154.63) * mm, "end": v(136.95, 154.9) * mm});
            skPoint(sketch, "E62.visualSharp", {"position": v(12.7, 193.26) * mm});
            skArc(sketch, "E62.filletArc", {"start": v(19.7, 192.67) * mm, "mid": v(14.8, 191.07) * mm, "end": v(12.7, 186.35) * mm});
            skPoint(sketch, "E63.visualSharp", {"position": v(127.67, 145.63) * mm});
            skArc(sketch, "E63.filletArc", {"start": v(122.8, 140.75) * mm, "mid": v(124.64, 145.57) * mm, "end": v(122.31, 150.17) * mm});
            skPoint(sketch, "E64.visualSharp", {"position": v(69.57, 87.53) * mm});
            skArc(sketch, "E64.filletArc", {"start": v(65.28, 90.77) * mm, "mid": v(69.5, 89.6) * mm, "end": v(73.48, 91.44) * mm});
            skPoint(sketch, "E65.visualSharp", {"position": v(12.7, 111.08) * mm});
            skArc(sketch, "E65.filletArc", {"start": v(12.7, 116.61) * mm, "mid": v(14.21, 112.5) * mm, "end": v(18.03, 110.35) * mm});
            skArc(sketch, "E66.1.0", {"start": v(-122.31, 150.17) * mm, "mid": v(-124.64, 145.57) * mm, "end": v(-122.8, 140.75) * mm});
            skArc(sketch, "E66.1.1", {"start": v(-19.7, 192.67) * mm, "mid": v(-74.12, 178.93) * mm, "end": v(-122.31, 150.17) * mm});
            skArc(sketch, "E66.1.2", {"start": v(-12.7, 186.35) * mm, "mid": v(-14.8, 191.07) * mm, "end": v(-19.7, 192.67) * mm});
            skLineSegment(sketch, "E66.1.3", {"start": v(-12.7, 116.61) * mm, "end": v(-12.7, 186.35) * mm});
            skArc(sketch, "E66.1.4", {"start": v(-18.03, 110.35) * mm, "mid": v(-14.21, 112.5) * mm, "end": v(-12.7, 116.61) * mm});
            skArc(sketch, "E66.1.5", {"start": v(-18.03, 110.35) * mm, "mid": v(-42.79, 103.3) * mm, "end": v(-65.28, 90.77) * mm});
            skArc(sketch, "E66.1.6", {"start": v(-73.48, 91.44) * mm, "mid": v(-69.5, 89.6) * mm, "end": v(-65.28, 90.77) * mm});
            skLineSegment(sketch, "E66.1.7", {"start": v(-73.48, 91.44) * mm, "end": v(-122.8, 140.75) * mm});
            skArc(sketch, "E66.2.0", {"start": v(-192.67, 19.7) * mm, "mid": v(-191.07, 14.8) * mm, "end": v(-186.35, 12.7) * mm});
            skArc(sketch, "E66.2.1", {"start": v(-150.17, 122.31) * mm, "mid": v(-178.93, 74.12) * mm, "end": v(-192.67, 19.7) * mm});
            skArc(sketch, "E66.2.2", {"start": v(-140.75, 122.8) * mm, "mid": v(-145.57, 124.64) * mm, "end": v(-150.17, 122.31) * mm});
            skLineSegment(sketch, "E66.2.3", {"start": v(-91.44, 73.48) * mm, "end": v(-140.75, 122.8) * mm});
            skArc(sketch, "E66.2.4", {"start": v(-90.77, 65.28) * mm, "mid": v(-89.6, 69.5) * mm, "end": v(-91.44, 73.48) * mm});
            skArc(sketch, "E66.2.5", {"start": v(-90.77, 65.28) * mm, "mid": v(-103.3, 42.79) * mm, "end": v(-110.35, 18.03) * mm});
            skArc(sketch, "E66.2.6", {"start": v(-116.61, 12.7) * mm, "mid": v(-112.5, 14.21) * mm, "end": v(-110.35, 18.03) * mm});
            skLineSegment(sketch, "E66.2.7", {"start": v(-116.61, 12.7) * mm, "end": v(-186.35, 12.7) * mm});
            skArc(sketch, "E66.3.0", {"start": v(-150.17, -122.31) * mm, "mid": v(-145.57, -124.64) * mm, "end": v(-140.75, -122.8) * mm});
            skArc(sketch, "E66.3.1", {"start": v(-192.67, -19.7) * mm, "mid": v(-178.93, -74.12) * mm, "end": v(-150.17, -122.31) * mm});
            skArc(sketch, "E66.3.2", {"start": v(-186.35, -12.7) * mm, "mid": v(-191.07, -14.8) * mm, "end": v(-192.67, -19.7) * mm});
            skLineSegment(sketch, "E66.3.3", {"start": v(-116.61, -12.7) * mm, "end": v(-186.35, -12.7) * mm});
            skArc(sketch, "E66.3.4", {"start": v(-110.35, -18.03) * mm, "mid": v(-112.5, -14.21) * mm, "end": v(-116.61, -12.7) * mm});
            skArc(sketch, "E66.3.5", {"start": v(-110.35, -18.03) * mm, "mid": v(-103.3, -42.79) * mm, "end": v(-90.77, -65.28) * mm});
            skArc(sketch, "E66.3.6", {"start": v(-91.44, -73.48) * mm, "mid": v(-89.6, -69.5) * mm, "end": v(-90.77, -65.28) * mm});
            skLineSegment(sketch, "E66.3.7", {"start": v(-91.44, -73.48) * mm, "end": v(-140.75, -122.8) * mm});
            skArc(sketch, "E66.4.0", {"start": v(-19.7, -192.67) * mm, "mid": v(-14.8, -191.07) * mm, "end": v(-12.7, -186.35) * mm});
            skArc(sketch, "E66.4.1", {"start": v(-122.31, -150.17) * mm, "mid": v(-74.12, -178.93) * mm, "end": v(-19.7, -192.67) * mm});
            skArc(sketch, "E66.4.2", {"start": v(-122.8, -140.75) * mm, "mid": v(-124.64, -145.57) * mm, "end": v(-122.31, -150.17) * mm});
            skLineSegment(sketch, "E66.4.3", {"start": v(-73.48, -91.44) * mm, "end": v(-122.8, -140.75) * mm});
            skArc(sketch, "E66.4.4", {"start": v(-65.28, -90.77) * mm, "mid": v(-69.5, -89.6) * mm, "end": v(-73.48, -91.44) * mm});
            skArc(sketch, "E66.4.5", {"start": v(-65.28, -90.77) * mm, "mid": v(-42.79, -103.3) * mm, "end": v(-18.03, -110.35) * mm});
            skArc(sketch, "E66.4.6", {"start": v(-12.7, -116.61) * mm, "mid": v(-14.21, -112.5) * mm, "end": v(-18.03, -110.35) * mm});
            skLineSegment(sketch, "E66.4.7", {"start": v(-12.7, -116.61) * mm, "end": v(-12.7, -186.35) * mm});
            skArc(sketch, "E66.5.0", {"start": v(122.31, -150.17) * mm, "mid": v(124.64, -145.57) * mm, "end": v(122.8, -140.75) * mm});
            skArc(sketch, "E66.5.1", {"start": v(19.7, -192.67) * mm, "mid": v(74.12, -178.93) * mm, "end": v(122.31, -150.17) * mm});
            skArc(sketch, "E66.5.2", {"start": v(12.7, -186.35) * mm, "mid": v(14.8, -191.07) * mm, "end": v(19.7, -192.67) * mm});
            skLineSegment(sketch, "E66.5.3", {"start": v(12.7, -116.61) * mm, "end": v(12.7, -186.35) * mm});
            skArc(sketch, "E66.5.4", {"start": v(18.03, -110.35) * mm, "mid": v(14.21, -112.5) * mm, "end": v(12.7, -116.61) * mm});
            skArc(sketch, "E66.5.5", {"start": v(18.03, -110.35) * mm, "mid": v(42.79, -103.3) * mm, "end": v(65.28, -90.77) * mm});
            skArc(sketch, "E66.5.6", {"start": v(73.48, -91.44) * mm, "mid": v(69.5, -89.6) * mm, "end": v(65.28, -90.77) * mm});
            skLineSegment(sketch, "E66.5.7", {"start": v(73.48, -91.44) * mm, "end": v(122.8, -140.75) * mm});
            skArc(sketch, "E66.6.0", {"start": v(192.67, -19.7) * mm, "mid": v(191.07, -14.8) * mm, "end": v(186.35, -12.7) * mm});
            skArc(sketch, "E66.6.1", {"start": v(150.17, -122.31) * mm, "mid": v(178.93, -74.12) * mm, "end": v(192.67, -19.7) * mm});
            skArc(sketch, "E66.6.2", {"start": v(140.75, -122.8) * mm, "mid": v(145.57, -124.64) * mm, "end": v(150.17, -122.31) * mm});
            skLineSegment(sketch, "E66.6.3", {"start": v(91.44, -73.48) * mm, "end": v(140.75, -122.8) * mm});
            skArc(sketch, "E66.6.4", {"start": v(90.77, -65.28) * mm, "mid": v(89.6, -69.5) * mm, "end": v(91.44, -73.48) * mm});
            skArc(sketch, "E66.6.5", {"start": v(90.77, -65.28) * mm, "mid": v(103.3, -42.79) * mm, "end": v(110.35, -18.03) * mm});
            skArc(sketch, "E66.6.6", {"start": v(116.61, -12.7) * mm, "mid": v(112.5, -14.21) * mm, "end": v(110.35, -18.03) * mm});
            skLineSegment(sketch, "E66.6.7", {"start": v(116.61, -12.7) * mm, "end": v(186.35, -12.7) * mm});
            skArc(sketch, "E66.7.0", {"start": v(150.17, 122.31) * mm, "mid": v(145.57, 124.64) * mm, "end": v(140.75, 122.8) * mm});
            skArc(sketch, "E66.7.1", {"start": v(192.67, 19.7) * mm, "mid": v(178.93, 74.12) * mm, "end": v(150.17, 122.31) * mm});
            skArc(sketch, "E66.7.2", {"start": v(186.35, 12.7) * mm, "mid": v(191.07, 14.8) * mm, "end": v(192.67, 19.7) * mm});
            skLineSegment(sketch, "E66.7.3", {"start": v(116.61, 12.7) * mm, "end": v(186.35, 12.7) * mm});
            skArc(sketch, "E66.7.4", {"start": v(110.35, 18.03) * mm, "mid": v(112.5, 14.21) * mm, "end": v(116.61, 12.7) * mm});
            skArc(sketch, "E66.7.5", {"start": v(110.35, 18.03) * mm, "mid": v(103.3, 42.79) * mm, "end": v(90.77, 65.28) * mm});
            skArc(sketch, "E66.7.6", {"start": v(91.44, 73.48) * mm, "mid": v(89.6, 69.5) * mm, "end": v(90.77, 65.28) * mm});
            skLineSegment(sketch, "E66.7.7", {"start": v(91.44, 73.48) * mm, "end": v(140.75, 122.8) * mm});
            skCircle(sketch, "E67", {"center": v(0, 0) * mm, "radius": 85.73 * mm});
            skLineSegment(sketch, "E68", {"start": v(-99.1, 0) * mm, "end": v(-206.38, 0) * mm});
            skLineSegment(sketch, "E69", {"start": v(99.1, 0) * mm, "end": v(206.38, 0) * mm});
            skLineSegment(sketch, "E70", {"start": v(0, -99.1) * mm, "end": v(0, -206.38) * mm});
            skSolve(sketch);
        }
        {
            var Q0;
            Q0=makeQuery(id+"F4.imprint","IMPRINT",FACE,{"disambiguationData":[TD([[makeQuery(id+"F4.imprint","IMPRINT",EDGE,{"derivedFrom":sQuery(id+"F4.wireOp",EDGE,"E46")}),1.0]])]});
            var Q1;
            {var subQ3=sQuery(id+"F4.wireOp",EDGE,"E54");Q1=makeQuery(id+"F4.imprint","IMPRINT",FACE,{"disambiguationData":[TD([[makeQuery(id+"F4.imprint","IMPRINT",EDGE,{"derivedFrom":subQ3}),1.0]])]});}
            var Q2;
            {var subQ4=sQuery(id+"F4.wireOp",EDGE,"E54");Q2=makeQuery(id+"F4.imprint","IMPRINT",FACE,{"disambiguationData":[TD([[makeQuery(id+"F4.imprint","IMPRINT",EDGE,{"derivedFrom":subQ4}),-1.0]])]});}
            var Q3;
            {var subQ0=sQuery(id+"F4.wireOp",EDGE,"E53.1.1");var subQ1=sQuery(id+"F4.wireOp",EDGE,"E47");var subQ2=makeQuery(id+"F4.imprint","INTERSECT",VERTEX,{"derivedFrom":[subQ1,subQ0]});Q3=makeQuery(id+"F4.imprint","IMPRINT",FACE,{"disambiguationData":[TD([[makeQuery(id+"F4.imprint","IMPRINT",EDGE,{"disambiguationData":[TD([[subQ2,1.0]])],"derivedFrom":subQ1}),1.0]])]});}
            var Q4;
            {var subQ0=sQuery(id+"F4.wireOp",EDGE,"E53.1.2");var subQ1=sQuery(id+"F4.wireOp",EDGE,"E47");var subQ2=makeQuery(id+"F4.imprint","INTERSECT",VERTEX,{"derivedFrom":[subQ1,subQ0]});Q4=makeQuery(id+"F4.imprint","IMPRINT",FACE,{"disambiguationData":[TD([[makeQuery(id+"F4.imprint","IMPRINT",EDGE,{"disambiguationData":[TD([[subQ2,1.0]])],"derivedFrom":subQ1}),1.0]])]});}
            var Q5;
            {var subQ0=sQuery(id+"F4.wireOp",EDGE,"E53.1.3");var subQ1=sQuery(id+"F4.wireOp",EDGE,"E47");var subQ2=makeQuery(id+"F4.imprint","INTERSECT",VERTEX,{"derivedFrom":[subQ1,subQ0]});Q5=makeQuery(id+"F4.imprint","IMPRINT",FACE,{"disambiguationData":[TD([[makeQuery(id+"F4.imprint","IMPRINT",EDGE,{"disambiguationData":[TD([[subQ2,1.0]])],"derivedFrom":subQ1}),1.0]])]});}
            var Q6;
            {var subQ1=sQuery(id+"F4.wireOp",EDGE,"E47");var subQ3=sQuery(id+"F4.wireOp",EDGE,"E53.1.4");var subQ4=makeQuery(id+"F4.imprint","INTERSECT",VERTEX,{"derivedFrom":[subQ1,subQ3]});Q6=makeQuery(id+"F4.imprint","IMPRINT",FACE,{"disambiguationData":[TD([[makeQuery(id+"F4.imprint","IMPRINT",EDGE,{"disambiguationData":[TD([[subQ4,1.0]])],"derivedFrom":subQ3}),-1.0]])]});}
            var Q7;
            {var subQ1=sQuery(id+"F4.wireOp",EDGE,"E47");var subQ3=sQuery(id+"F4.wireOp",EDGE,"E49");var subQ4=makeQuery(id+"F4.imprint","INTERSECT",VERTEX,{"derivedFrom":[subQ1,subQ3]});Q7=makeQuery(id+"F4.imprint","IMPRINT",FACE,{"disambiguationData":[TD([[makeQuery(id+"F4.imprint","IMPRINT",EDGE,{"disambiguationData":[TD([[subQ4,1.0]])],"derivedFrom":subQ3}),1.0]])]});}
            var Q8;
            {var subQ0=sQuery(id+"F4.wireOp",EDGE,"E49");var subQ1=sQuery(id+"F4.wireOp",EDGE,"E47");var subQ2=makeQuery(id+"F4.imprint","INTERSECT",VERTEX,{"derivedFrom":[subQ1,subQ0]});Q8=makeQuery(id+"F4.imprint","IMPRINT",FACE,{"disambiguationData":[TD([[makeQuery(id+"F4.imprint","IMPRINT",EDGE,{"disambiguationData":[TD([[subQ2,1.0]])],"derivedFrom":subQ1}),1.0]])]});}
            var Q9;
            {var subQ1=sQuery(id+"F4.wireOp",EDGE,"E47");var subQ4=sQuery(id+"F4.wireOp",EDGE,"E51");var subQ5=makeQuery(id+"F4.imprint","INTERSECT",VERTEX,{"derivedFrom":[subQ1,subQ4]});Q9=makeQuery(id+"F4.imprint","IMPRINT",FACE,{"disambiguationData":[TD([[makeQuery(id+"F4.imprint","IMPRINT",EDGE,{"disambiguationData":[TD([[subQ5,-1.0]])],"derivedFrom":subQ1}),1.0]])]});}
            var Q10;
            {var subQ0=sQuery(id+"F4.wireOp",EDGE,"E51");var subQ1=sQuery(id+"F4.wireOp",EDGE,"E47");var subQ2=makeQuery(id+"F4.imprint","INTERSECT",VERTEX,{"derivedFrom":[subQ1,subQ0]});Q10=makeQuery(id+"F4.imprint","IMPRINT",FACE,{"disambiguationData":[TD([[makeQuery(id+"F4.imprint","IMPRINT",EDGE,{"disambiguationData":[TD([[subQ2,1.0]])],"derivedFrom":subQ1}),1.0]])]});}
            var Q11;
            {var subQ0=sQuery(id+"F4.wireOp",EDGE,"E52");var subQ1=sQuery(id+"F4.wireOp",EDGE,"E47");var subQ2=makeQuery(id+"F4.imprint","INTERSECT",VERTEX,{"derivedFrom":[subQ1,subQ0]});Q11=makeQuery(id+"F4.imprint","IMPRINT",FACE,{"disambiguationData":[TD([[makeQuery(id+"F4.imprint","IMPRINT",EDGE,{"disambiguationData":[TD([[subQ2,1.0]])],"derivedFrom":subQ1}),1.0]])]});}
            var Q12;
            {var subQ0=sQuery(id+"F4.wireOp",EDGE,"E53.3.0");var subQ1=sQuery(id+"F4.wireOp",EDGE,"E47");var subQ2=makeQuery(id+"F4.imprint","INTERSECT",VERTEX,{"derivedFrom":[subQ1,subQ0]});Q12=makeQuery(id+"F4.imprint","IMPRINT",FACE,{"disambiguationData":[TD([[makeQuery(id+"F4.imprint","IMPRINT",EDGE,{"disambiguationData":[TD([[subQ2,1.0]])],"derivedFrom":subQ1}),1.0]])]});}
            var Q13;
            {var subQ0=sQuery(id+"F4.wireOp",EDGE,"E53.3.1");var subQ1=sQuery(id+"F4.wireOp",EDGE,"E47");var subQ2=makeQuery(id+"F4.imprint","INTERSECT",VERTEX,{"derivedFrom":[subQ1,subQ0]});Q13=makeQuery(id+"F4.imprint","IMPRINT",FACE,{"disambiguationData":[TD([[makeQuery(id+"F4.imprint","IMPRINT",EDGE,{"disambiguationData":[TD([[subQ2,1.0]])],"derivedFrom":subQ1}),1.0]])]});}
            var Q14;
            {var subQ0=sQuery(id+"F4.wireOp",EDGE,"E53.3.2");var subQ1=sQuery(id+"F4.wireOp",EDGE,"E47");var subQ2=makeQuery(id+"F4.imprint","INTERSECT",VERTEX,{"derivedFrom":[subQ1,subQ0]});Q14=makeQuery(id+"F4.imprint","IMPRINT",FACE,{"disambiguationData":[TD([[makeQuery(id+"F4.imprint","IMPRINT",EDGE,{"disambiguationData":[TD([[subQ2,1.0]])],"derivedFrom":subQ1}),1.0]])]});}
            var Q15;
            {var subQ0=sQuery(id+"F4.wireOp",EDGE,"E53.3.3");var subQ1=sQuery(id+"F4.wireOp",EDGE,"E47");var subQ2=makeQuery(id+"F4.imprint","INTERSECT",VERTEX,{"derivedFrom":[subQ1,subQ0]});Q15=makeQuery(id+"F4.imprint","IMPRINT",FACE,{"disambiguationData":[TD([[makeQuery(id+"F4.imprint","IMPRINT",EDGE,{"disambiguationData":[TD([[subQ2,1.0]])],"derivedFrom":subQ1}),1.0]])]});}
            var Q16;
            {var subQ0=sQuery(id+"F4.wireOp",EDGE,"E53.2.0");var subQ1=sQuery(id+"F4.wireOp",EDGE,"E47");var subQ2=makeQuery(id+"F4.imprint","INTERSECT",VERTEX,{"derivedFrom":[subQ1,subQ0]});Q16=makeQuery(id+"F4.imprint","IMPRINT",FACE,{"disambiguationData":[TD([[makeQuery(id+"F4.imprint","IMPRINT",EDGE,{"disambiguationData":[TD([[subQ2,-1.0]])],"derivedFrom":subQ1}),1.0]])]});}
            var Q17;
            {var subQ0=sQuery(id+"F4.wireOp",EDGE,"E53.2.0");var subQ1=sQuery(id+"F4.wireOp",EDGE,"E47");var subQ2=makeQuery(id+"F4.imprint","INTERSECT",VERTEX,{"derivedFrom":[subQ1,subQ0]});Q17=makeQuery(id+"F4.imprint","IMPRINT",FACE,{"disambiguationData":[TD([[makeQuery(id+"F4.imprint","IMPRINT",EDGE,{"disambiguationData":[TD([[subQ2,1.0]])],"derivedFrom":subQ1}),1.0]])]});}
            var Q18;
            {var subQ0=sQuery(id+"F4.wireOp",EDGE,"E53.2.1");var subQ1=sQuery(id+"F4.wireOp",EDGE,"E47");var subQ2=makeQuery(id+"F4.imprint","INTERSECT",VERTEX,{"derivedFrom":[subQ1,subQ0]});Q18=makeQuery(id+"F4.imprint","IMPRINT",FACE,{"disambiguationData":[TD([[makeQuery(id+"F4.imprint","IMPRINT",EDGE,{"disambiguationData":[TD([[subQ2,1.0]])],"derivedFrom":subQ1}),1.0]])]});}
            var Q19;
            {var subQ0=sQuery(id+"F4.wireOp",EDGE,"E53.2.2");var subQ1=sQuery(id+"F4.wireOp",EDGE,"E47");var subQ2=makeQuery(id+"F4.imprint","INTERSECT",VERTEX,{"derivedFrom":[subQ1,subQ0]});Q19=makeQuery(id+"F4.imprint","IMPRINT",FACE,{"disambiguationData":[TD([[makeQuery(id+"F4.imprint","IMPRINT",EDGE,{"disambiguationData":[TD([[subQ2,1.0]])],"derivedFrom":subQ1}),1.0]])]});}
            var Q20;
            {var subQ0=sQuery(id+"F4.wireOp",EDGE,"E53.2.3");var subQ1=sQuery(id+"F4.wireOp",EDGE,"E47");var subQ2=makeQuery(id+"F4.imprint","INTERSECT",VERTEX,{"derivedFrom":[subQ1,subQ0]});Q20=makeQuery(id+"F4.imprint","IMPRINT",FACE,{"disambiguationData":[TD([[makeQuery(id+"F4.imprint","IMPRINT",EDGE,{"disambiguationData":[TD([[subQ2,1.0]])],"derivedFrom":subQ1}),1.0]])]});}
            var Q21;
            {var subQ0=sQuery(id+"F4.wireOp",EDGE,"E53.1.0");var subQ1=sQuery(id+"F4.wireOp",EDGE,"E47");var subQ2=makeQuery(id+"F4.imprint","INTERSECT",VERTEX,{"derivedFrom":[subQ1,subQ0]});Q21=makeQuery(id+"F4.imprint","IMPRINT",FACE,{"disambiguationData":[TD([[makeQuery(id+"F4.imprint","IMPRINT",EDGE,{"disambiguationData":[TD([[subQ2,-1.0]])],"derivedFrom":subQ1}),1.0]])]});}
            var Q22;
            {var subQ0=sQuery(id+"F4.wireOp",EDGE,"E53.1.0");var subQ1=sQuery(id+"F4.wireOp",EDGE,"E47");var subQ2=makeQuery(id+"F4.imprint","INTERSECT",VERTEX,{"derivedFrom":[subQ1,subQ0]});Q22=makeQuery(id+"F4.imprint","IMPRINT",FACE,{"disambiguationData":[TD([[makeQuery(id+"F4.imprint","IMPRINT",EDGE,{"disambiguationData":[TD([[subQ2,1.0]])],"derivedFrom":subQ1}),1.0]])]});}
            var Q23;
            Q23=makeQuery(id+"F4.imprint","IMPRINT",FACE,{"disambiguationData":[TD([[makeQuery(id+"F4.imprint","IMPRINT",EDGE,{"derivedFrom":sQuery(id+"F4.wireOp",EDGE,"E66.3.0")}),-1.0]])]});
            var Q24;
            Q24=makeQuery(id+"F4.imprint","IMPRINT",FACE,{"disambiguationData":[TD([[makeQuery(id+"F4.imprint","IMPRINT",EDGE,{"derivedFrom":sQuery(id+"F4.wireOp",EDGE,"E66.5.0")}),-1.0]])]});
            var Q25;
            {var subQ0=sQuery(id+"F4.wireOp",EDGE,"E55");Q25=makeQuery(id+"F4.imprint","IMPRINT",FACE,{"disambiguationData":[TD([[makeQuery(id+"F4.imprint","IMPRINT",EDGE,{"derivedFrom":subQ0}),-1.0]])]});}
            extrude(context, id + "F5", {"entities" : qUnion([Q0, Q1, Q2, Q3, Q4, Q5, Q6, Q7, Q8, Q9, Q10, Q11, Q12, Q13, Q14, Q15, Q16, Q17, Q18, Q19, Q20, Q21, Q22, Q23, Q24, Q25]), "depth" : 9.52 * mm});
        }
        {
            var Q0;
            Q0=sQuery(id+"F4.wireOp",VERTEX,"E68.end");
            var Q1;
            Q1=sQuery(id+"F4.wireOp",VERTEX,"E70.end");
            var Q2;
            Q2=sQuery(id+"F4.wireOp",VERTEX,"E69.end");
            var Q3;
            Q3=sQuery(id+"F4.wireOp",VERTEX,"E54.end");
            var Q4;
            Q4=makeQuery(id+"F5.opExtrude","SWEPT_BODY",BODY,{"disambiguationData":[OSD([sQuery(id+"F4.wireOp",EDGE,"E46"),sQuery(id+"F4.wireOp",EDGE,"E56.0"),sQuery(id+"F4.wireOp",EDGE,"E57.0"),sQuery(id+"F4.wireOp",EDGE,"E58.0"),sQuery(id+"F4.wireOp",EDGE,"E59.0"),sQuery(id+"F4.wireOp",EDGE,"E62.filletArc"),sQuery(id+"F4.wireOp",EDGE,"E63.filletArc"),sQuery(id+"F4.wireOp",EDGE,"E64.filletArc"),sQuery(id+"F4.wireOp",EDGE,"E65.filletArc"),sQuery(id+"F4.wireOp",EDGE,"E66.1.0"),sQuery(id+"F4.wireOp",EDGE,"E66.1.1"),sQuery(id+"F4.wireOp",EDGE,"E66.1.2"),sQuery(id+"F4.wireOp",EDGE,"E66.1.3"),sQuery(id+"F4.wireOp",EDGE,"E66.1.4"),sQuery(id+"F4.wireOp",EDGE,"E66.1.5"),sQuery(id+"F4.wireOp",EDGE,"E66.1.6"),sQuery(id+"F4.wireOp",EDGE,"E66.1.7"),sQuery(id+"F4.wireOp",EDGE,"E66.2.0"),sQuery(id+"F4.wireOp",EDGE,"E66.2.1"),sQuery(id+"F4.wireOp",EDGE,"E66.2.2"),sQuery(id+"F4.wireOp",EDGE,"E66.2.3"),sQuery(id+"F4.wireOp",EDGE,"E66.2.4"),sQuery(id+"F4.wireOp",EDGE,"E66.2.5"),sQuery(id+"F4.wireOp",EDGE,"E66.2.6"),sQuery(id+"F4.wireOp",EDGE,"E66.2.7"),sQuery(id+"F4.wireOp",EDGE,"E66.3.0"),sQuery(id+"F4.wireOp",EDGE,"E66.3.1"),sQuery(id+"F4.wireOp",EDGE,"E66.3.2"),sQuery(id+"F4.wireOp",EDGE,"E66.3.3"),sQuery(id+"F4.wireOp",EDGE,"E66.3.4"),sQuery(id+"F4.wireOp",EDGE,"E66.3.5"),sQuery(id+"F4.wireOp",EDGE,"E66.3.6"),sQuery(id+"F4.wireOp",EDGE,"E66.3.7"),sQuery(id+"F4.wireOp",EDGE,"E66.4.0"),sQuery(id+"F4.wireOp",EDGE,"E66.4.1"),sQuery(id+"F4.wireOp",EDGE,"E66.4.2"),sQuery(id+"F4.wireOp",EDGE,"E66.4.3"),sQuery(id+"F4.wireOp",EDGE,"E66.4.4"),sQuery(id+"F4.wireOp",EDGE,"E66.4.5"),sQuery(id+"F4.wireOp",EDGE,"E66.4.6"),sQuery(id+"F4.wireOp",EDGE,"E66.4.7"),sQuery(id+"F4.wireOp",EDGE,"E66.5.0"),sQuery(id+"F4.wireOp",EDGE,"E66.5.1"),sQuery(id+"F4.wireOp",EDGE,"E66.5.2"),sQuery(id+"F4.wireOp",EDGE,"E66.5.3"),sQuery(id+"F4.wireOp",EDGE,"E66.5.4"),sQuery(id+"F4.wireOp",EDGE,"E66.5.5"),sQuery(id+"F4.wireOp",EDGE,"E66.5.6"),sQuery(id+"F4.wireOp",EDGE,"E66.5.7"),sQuery(id+"F4.wireOp",EDGE,"E66.6.0"),sQuery(id+"F4.wireOp",EDGE,"E66.6.1"),sQuery(id+"F4.wireOp",EDGE,"E66.6.2"),sQuery(id+"F4.wireOp",EDGE,"E66.6.3"),sQuery(id+"F4.wireOp",EDGE,"E66.6.4"),sQuery(id+"F4.wireOp",EDGE,"E66.6.5"),sQuery(id+"F4.wireOp",EDGE,"E66.6.6"),sQuery(id+"F4.wireOp",EDGE,"E66.6.7"),sQuery(id+"F4.wireOp",EDGE,"E66.7.0"),sQuery(id+"F4.wireOp",EDGE,"E66.7.1"),sQuery(id+"F4.wireOp",EDGE,"E66.7.2"),sQuery(id+"F4.wireOp",EDGE,"E66.7.3"),sQuery(id+"F4.wireOp",EDGE,"E66.7.4"),sQuery(id+"F4.wireOp",EDGE,"E66.7.5"),sQuery(id+"F4.wireOp",EDGE,"E66.7.6"),sQuery(id+"F4.wireOp",EDGE,"E66.7.7"),sQuery(id+"F4.wireOp",EDGE,"E67")])]});
            hole(context, id + "F6", {"style" : HoleStyle.SIMPLE, "endStyle" : HoleEndStyle.BLIND, "oppositeDirection" : true, "standardTappedOrClearance" : lookupTablePath({ "standard" : "ANSI", "fit" : "Close", "size" : "1/2", "type" : "Clearance" }), "standardBlindInLast" : lookupTablePath({ "fit" : "Close", "standard" : "ANSI", "size" : "1/2", "type" : "Clearance" }), "holeDiameter" : 13.1 * mm, "holeDepth" : 5.08 * mm, "locations" : qUnion([Q0, Q1, Q2, Q3]), "scope" : qUnion([Q4])});
        }
        {
            var Q0;
            Q0=sQuery(id+"F4.wireOp",VERTEX,"E48.end");
            var Q1;
            Q1=sQuery(id+"F4.wireOp",VERTEX,"E53.1.4.end");
            var Q2;
            Q2=sQuery(id+"F4.wireOp",VERTEX,"E53.1.3.end");
            var Q3;
            Q3=sQuery(id+"F4.wireOp",VERTEX,"E53.1.2.end");
            var Q4;
            Q4=sQuery(id+"F4.wireOp",VERTEX,"E53.1.1.end");
            var Q5;
            Q5=sQuery(id+"F4.wireOp",VERTEX,"E53.1.0.end");
            var Q6;
            Q6=sQuery(id+"F4.wireOp",VERTEX,"E53.2.4.end");
            var Q7;
            Q7=sQuery(id+"F4.wireOp",VERTEX,"E53.2.3.end");
            var Q8;
            Q8=sQuery(id+"F4.wireOp",VERTEX,"E53.2.2.end");
            var Q9;
            Q9=sQuery(id+"F4.wireOp",VERTEX,"E53.2.1.end");
            var Q10;
            Q10=sQuery(id+"F4.wireOp",VERTEX,"E53.2.0.end");
            var Q11;
            Q11=sQuery(id+"F4.wireOp",VERTEX,"E53.3.4.end");
            var Q12;
            Q12=sQuery(id+"F4.wireOp",VERTEX,"E53.3.3.end");
            var Q13;
            Q13=sQuery(id+"F4.wireOp",VERTEX,"E53.3.2.end");
            var Q14;
            Q14=sQuery(id+"F4.wireOp",VERTEX,"E53.3.1.end");
            var Q15;
            Q15=sQuery(id+"F4.wireOp",VERTEX,"E69.start");
            var Q16;
            Q16=sQuery(id+"F4.wireOp",VERTEX,"E52.end");
            var Q17;
            Q17=sQuery(id+"F4.wireOp",VERTEX,"E51.end");
            var Q18;
            Q18=sQuery(id+"F4.wireOp",VERTEX,"E50.end");
            var Q19;
            Q19=sQuery(id+"F4.wireOp",VERTEX,"E49.end");
            var Q20;
            Q20=makeQuery(id+"F5.opExtrude","SWEPT_BODY",BODY,{"disambiguationData":[OSD([sQuery(id+"F4.wireOp",EDGE,"E46"),sQuery(id+"F4.wireOp",EDGE,"E56.0"),sQuery(id+"F4.wireOp",EDGE,"E57.0"),sQuery(id+"F4.wireOp",EDGE,"E58.0"),sQuery(id+"F4.wireOp",EDGE,"E59.0"),sQuery(id+"F4.wireOp",EDGE,"E62.filletArc"),sQuery(id+"F4.wireOp",EDGE,"E63.filletArc"),sQuery(id+"F4.wireOp",EDGE,"E64.filletArc"),sQuery(id+"F4.wireOp",EDGE,"E65.filletArc"),sQuery(id+"F4.wireOp",EDGE,"E66.1.0"),sQuery(id+"F4.wireOp",EDGE,"E66.1.1"),sQuery(id+"F4.wireOp",EDGE,"E66.1.2"),sQuery(id+"F4.wireOp",EDGE,"E66.1.3"),sQuery(id+"F4.wireOp",EDGE,"E66.1.4"),sQuery(id+"F4.wireOp",EDGE,"E66.1.5"),sQuery(id+"F4.wireOp",EDGE,"E66.1.6"),sQuery(id+"F4.wireOp",EDGE,"E66.1.7"),sQuery(id+"F4.wireOp",EDGE,"E66.2.0"),sQuery(id+"F4.wireOp",EDGE,"E66.2.1"),sQuery(id+"F4.wireOp",EDGE,"E66.2.2"),sQuery(id+"F4.wireOp",EDGE,"E66.2.3"),sQuery(id+"F4.wireOp",EDGE,"E66.2.4"),sQuery(id+"F4.wireOp",EDGE,"E66.2.5"),sQuery(id+"F4.wireOp",EDGE,"E66.2.6"),sQuery(id+"F4.wireOp",EDGE,"E66.2.7"),sQuery(id+"F4.wireOp",EDGE,"E66.3.0"),sQuery(id+"F4.wireOp",EDGE,"E66.3.1"),sQuery(id+"F4.wireOp",EDGE,"E66.3.2"),sQuery(id+"F4.wireOp",EDGE,"E66.3.3"),sQuery(id+"F4.wireOp",EDGE,"E66.3.4"),sQuery(id+"F4.wireOp",EDGE,"E66.3.5"),sQuery(id+"F4.wireOp",EDGE,"E66.3.6"),sQuery(id+"F4.wireOp",EDGE,"E66.3.7"),sQuery(id+"F4.wireOp",EDGE,"E66.4.0"),sQuery(id+"F4.wireOp",EDGE,"E66.4.1"),sQuery(id+"F4.wireOp",EDGE,"E66.4.2"),sQuery(id+"F4.wireOp",EDGE,"E66.4.3"),sQuery(id+"F4.wireOp",EDGE,"E66.4.4"),sQuery(id+"F4.wireOp",EDGE,"E66.4.5"),sQuery(id+"F4.wireOp",EDGE,"E66.4.6"),sQuery(id+"F4.wireOp",EDGE,"E66.4.7"),sQuery(id+"F4.wireOp",EDGE,"E66.5.0"),sQuery(id+"F4.wireOp",EDGE,"E66.5.1"),sQuery(id+"F4.wireOp",EDGE,"E66.5.2"),sQuery(id+"F4.wireOp",EDGE,"E66.5.3"),sQuery(id+"F4.wireOp",EDGE,"E66.5.4"),sQuery(id+"F4.wireOp",EDGE,"E66.5.5"),sQuery(id+"F4.wireOp",EDGE,"E66.5.6"),sQuery(id+"F4.wireOp",EDGE,"E66.5.7"),sQuery(id+"F4.wireOp",EDGE,"E66.6.0"),sQuery(id+"F4.wireOp",EDGE,"E66.6.1"),sQuery(id+"F4.wireOp",EDGE,"E66.6.2"),sQuery(id+"F4.wireOp",EDGE,"E66.6.3"),sQuery(id+"F4.wireOp",EDGE,"E66.6.4"),sQuery(id+"F4.wireOp",EDGE,"E66.6.5"),sQuery(id+"F4.wireOp",EDGE,"E66.6.6"),sQuery(id+"F4.wireOp",EDGE,"E66.6.7"),sQuery(id+"F4.wireOp",EDGE,"E66.7.0"),sQuery(id+"F4.wireOp",EDGE,"E66.7.1"),sQuery(id+"F4.wireOp",EDGE,"E66.7.2"),sQuery(id+"F4.wireOp",EDGE,"E66.7.3"),sQuery(id+"F4.wireOp",EDGE,"E66.7.4"),sQuery(id+"F4.wireOp",EDGE,"E66.7.5"),sQuery(id+"F4.wireOp",EDGE,"E66.7.6"),sQuery(id+"F4.wireOp",EDGE,"E66.7.7"),sQuery(id+"F4.wireOp",EDGE,"E67")])]});
            hole(context, id + "F7", {"style" : HoleStyle.SIMPLE, "endStyle" : HoleEndStyle.BLIND, "oppositeDirection" : true, "standardTappedOrClearance" : lookupTablePath({ "standard" : "ANSI", "fit" : "Close", "size" : "1/4", "type" : "Clearance" }), "standardBlindInLast" : lookupTablePath({ "fit" : "Close", "standard" : "ANSI", "size" : "1/4", "type" : "Clearance" }), "holeDiameter" : 6.53 * mm, "holeDepth" : 5.08 * mm, "locations" : qUnion([Q0, Q1, Q2, Q3, Q4, Q5, Q6, Q7, Q8, Q9, Q10, Q11, Q12, Q13, Q14, Q15, Q16, Q17, Q18, Q19]), "scope" : qUnion([Q20])});
        }
        {
            var Q0;
            Q0=makeQuery(id+"F5.opExtrude","CAP_FACE",FACE,{"disambiguationData":[OSD([sQuery(id+"F4.wireOp",EDGE,"E46"),sQuery(id+"F4.wireOp",EDGE,"E56.0"),sQuery(id+"F4.wireOp",EDGE,"E57.0"),sQuery(id+"F4.wireOp",EDGE,"E58.0"),sQuery(id+"F4.wireOp",EDGE,"E59.0"),sQuery(id+"F4.wireOp",EDGE,"E62.filletArc"),sQuery(id+"F4.wireOp",EDGE,"E63.filletArc"),sQuery(id+"F4.wireOp",EDGE,"E64.filletArc"),sQuery(id+"F4.wireOp",EDGE,"E65.filletArc"),sQuery(id+"F4.wireOp",EDGE,"E66.1.0"),sQuery(id+"F4.wireOp",EDGE,"E66.1.1"),sQuery(id+"F4.wireOp",EDGE,"E66.1.2"),sQuery(id+"F4.wireOp",EDGE,"E66.1.3"),sQuery(id+"F4.wireOp",EDGE,"E66.1.4"),sQuery(id+"F4.wireOp",EDGE,"E66.1.5"),sQuery(id+"F4.wireOp",EDGE,"E66.1.6"),sQuery(id+"F4.wireOp",EDGE,"E66.1.7"),sQuery(id+"F4.wireOp",EDGE,"E66.2.0"),sQuery(id+"F4.wireOp",EDGE,"E66.2.1"),sQuery(id+"F4.wireOp",EDGE,"E66.2.2"),sQuery(id+"F4.wireOp",EDGE,"E66.2.3"),sQuery(id+"F4.wireOp",EDGE,"E66.2.4"),sQuery(id+"F4.wireOp",EDGE,"E66.2.5"),sQuery(id+"F4.wireOp",EDGE,"E66.2.6"),sQuery(id+"F4.wireOp",EDGE,"E66.2.7"),sQuery(id+"F4.wireOp",EDGE,"E66.3.0"),sQuery(id+"F4.wireOp",EDGE,"E66.3.1"),sQuery(id+"F4.wireOp",EDGE,"E66.3.2"),sQuery(id+"F4.wireOp",EDGE,"E66.3.3"),sQuery(id+"F4.wireOp",EDGE,"E66.3.4"),sQuery(id+"F4.wireOp",EDGE,"E66.3.5"),sQuery(id+"F4.wireOp",EDGE,"E66.3.6"),sQuery(id+"F4.wireOp",EDGE,"E66.3.7"),sQuery(id+"F4.wireOp",EDGE,"E66.4.0"),sQuery(id+"F4.wireOp",EDGE,"E66.4.1"),sQuery(id+"F4.wireOp",EDGE,"E66.4.2"),sQuery(id+"F4.wireOp",EDGE,"E66.4.3"),sQuery(id+"F4.wireOp",EDGE,"E66.4.4"),sQuery(id+"F4.wireOp",EDGE,"E66.4.5"),sQuery(id+"F4.wireOp",EDGE,"E66.4.6"),sQuery(id+"F4.wireOp",EDGE,"E66.4.7"),sQuery(id+"F4.wireOp",EDGE,"E66.5.0"),sQuery(id+"F4.wireOp",EDGE,"E66.5.1"),sQuery(id+"F4.wireOp",EDGE,"E66.5.2"),sQuery(id+"F4.wireOp",EDGE,"E66.5.3"),sQuery(id+"F4.wireOp",EDGE,"E66.5.4"),sQuery(id+"F4.wireOp",EDGE,"E66.5.5"),sQuery(id+"F4.wireOp",EDGE,"E66.5.6"),sQuery(id+"F4.wireOp",EDGE,"E66.5.7"),sQuery(id+"F4.wireOp",EDGE,"E66.6.0"),sQuery(id+"F4.wireOp",EDGE,"E66.6.1"),sQuery(id+"F4.wireOp",EDGE,"E66.6.2"),sQuery(id+"F4.wireOp",EDGE,"E66.6.3"),sQuery(id+"F4.wireOp",EDGE,"E66.6.4"),sQuery(id+"F4.wireOp",EDGE,"E66.6.5"),sQuery(id+"F4.wireOp",EDGE,"E66.6.6"),sQuery(id+"F4.wireOp",EDGE,"E66.6.7"),sQuery(id+"F4.wireOp",EDGE,"E66.7.0"),sQuery(id+"F4.wireOp",EDGE,"E66.7.1"),sQuery(id+"F4.wireOp",EDGE,"E66.7.2"),sQuery(id+"F4.wireOp",EDGE,"E66.7.3"),sQuery(id+"F4.wireOp",EDGE,"E66.7.4"),sQuery(id+"F4.wireOp",EDGE,"E66.7.5"),sQuery(id+"F4.wireOp",EDGE,"E66.7.6"),sQuery(id+"F4.wireOp",EDGE,"E66.7.7"),sQuery(id+"F4.wireOp",EDGE,"E67")])],"isStart":false});
            var sketch = newSketch(context, id + "F8", { "sketchPlane" : qUnion([Q0])});
            skLineSegment(sketch, "E71", {"start": v(0, 0) * mm, "end": v(168.83, 168.83) * mm});
            skLineSegment(sketch, "E72", {"start": v(168.83, 168.83) * mm, "end": v(177.8, 159.85) * mm});
            skLineSegment(sketch, "E73", {"start": v(168.83, 168.83) * mm, "end": v(159.85, 177.8) * mm});
            skLineSegment(sketch, "E74", {"start": v(159.85, 177.8) * mm, "end": v(153.11, 171.07) * mm});
            skLineSegment(sketch, "E75", {"start": v(159.85, 177.8) * mm, "end": v(166.58, 184.54) * mm});
            skLineSegment(sketch, "E76.MirrorCS", {"start": v(177.8, 159.85) * mm, "end": v(184.54, 166.58) * mm});
            skLineSegment(sketch, "E77.MirrorCS", {"start": v(177.8, 159.85) * mm, "end": v(171.07, 153.11) * mm});
            skLineSegment(sketch, "E78.1.0", {"start": v(0, 0) * mm, "end": v(-168.83, 168.83) * mm});
            skLineSegment(sketch, "E78.1.1", {"start": v(-177.8, 159.85) * mm, "end": v(-184.54, 166.58) * mm});
            skLineSegment(sketch, "E78.1.2", {"start": v(-177.8, 159.85) * mm, "end": v(-171.07, 153.11) * mm});
            skLineSegment(sketch, "E78.1.3", {"start": v(-159.85, 177.8) * mm, "end": v(-166.58, 184.54) * mm});
            skLineSegment(sketch, "E78.1.4", {"start": v(-159.85, 177.8) * mm, "end": v(-153.11, 171.07) * mm});
            skLineSegment(sketch, "E78.2.0", {"start": v(0, 0) * mm, "end": v(-168.83, -168.83) * mm});
            skLineSegment(sketch, "E78.2.1", {"start": v(-159.85, -177.8) * mm, "end": v(-166.58, -184.54) * mm});
            skLineSegment(sketch, "E78.2.2", {"start": v(-159.85, -177.8) * mm, "end": v(-153.11, -171.07) * mm});
            skLineSegment(sketch, "E78.2.3", {"start": v(-177.8, -159.85) * mm, "end": v(-184.54, -166.58) * mm});
            skLineSegment(sketch, "E78.2.4", {"start": v(-177.8, -159.85) * mm, "end": v(-171.07, -153.11) * mm});
            skLineSegment(sketch, "E78.3.0", {"start": v(0, 0) * mm, "end": v(168.83, -168.83) * mm});
            skLineSegment(sketch, "E78.3.1", {"start": v(177.8, -159.85) * mm, "end": v(184.54, -166.58) * mm});
            skLineSegment(sketch, "E78.3.2", {"start": v(177.8, -159.85) * mm, "end": v(171.07, -153.11) * mm});
            skLineSegment(sketch, "E78.3.3", {"start": v(159.85, -177.8) * mm, "end": v(166.58, -184.54) * mm});
            skLineSegment(sketch, "E78.3.4", {"start": v(159.85, -177.8) * mm, "end": v(153.11, -171.07) * mm});
            skPoint(sketch, "E78.center", {"position": v(0, 0) * mm});
            skSolve(sketch);
        }
        {
            var Q0;
            Q0=sQuery(id+"F8.wireOp",VERTEX,"E78.1.1.end");
            var Q1;
            Q1=sQuery(id+"F8.wireOp",VERTEX,"E78.1.3.end");
            var Q2;
            Q2=sQuery(id+"F8.wireOp",VERTEX,"E78.1.4.end");
            var Q3;
            Q3=sQuery(id+"F8.wireOp",VERTEX,"E78.1.2.end");
            var Q4;
            Q4=sQuery(id+"F8.wireOp",VERTEX,"E74.end");
            var Q5;
            Q5=sQuery(id+"F8.wireOp",VERTEX,"E75.end");
            var Q6;
            Q6=sQuery(id+"F8.wireOp",VERTEX,"E76.MirrorCS.end");
            var Q7;
            Q7=sQuery(id+"F8.wireOp",VERTEX,"E77.MirrorCS.end");
            var Q8;
            Q8=sQuery(id+"F8.wireOp",VERTEX,"E78.3.3.end");
            var Q9;
            Q9=sQuery(id+"F8.wireOp",VERTEX,"E78.3.1.end");
            var Q10;
            Q10=sQuery(id+"F8.wireOp",VERTEX,"E78.3.2.end");
            var Q11;
            Q11=sQuery(id+"F8.wireOp",VERTEX,"E78.3.4.end");
            var Q12;
            Q12=sQuery(id+"F8.wireOp",VERTEX,"E78.2.1.end");
            var Q13;
            Q13=sQuery(id+"F8.wireOp",VERTEX,"E78.2.2.end");
            var Q14;
            Q14=sQuery(id+"F8.wireOp",VERTEX,"E78.2.4.end");
            var Q15;
            Q15=sQuery(id+"F8.wireOp",VERTEX,"E78.2.3.end");
            var Q16;
            Q16=makeQuery(id+"F5.opExtrude","SWEPT_BODY",BODY,{"disambiguationData":[OSD([sQuery(id+"F4.wireOp",EDGE,"E46"),sQuery(id+"F4.wireOp",EDGE,"E56.0"),sQuery(id+"F4.wireOp",EDGE,"E57.0"),sQuery(id+"F4.wireOp",EDGE,"E58.0"),sQuery(id+"F4.wireOp",EDGE,"E59.0"),sQuery(id+"F4.wireOp",EDGE,"E62.filletArc"),sQuery(id+"F4.wireOp",EDGE,"E63.filletArc"),sQuery(id+"F4.wireOp",EDGE,"E64.filletArc"),sQuery(id+"F4.wireOp",EDGE,"E65.filletArc"),sQuery(id+"F4.wireOp",EDGE,"E66.1.0"),sQuery(id+"F4.wireOp",EDGE,"E66.1.1"),sQuery(id+"F4.wireOp",EDGE,"E66.1.2"),sQuery(id+"F4.wireOp",EDGE,"E66.1.3"),sQuery(id+"F4.wireOp",EDGE,"E66.1.4"),sQuery(id+"F4.wireOp",EDGE,"E66.1.5"),sQuery(id+"F4.wireOp",EDGE,"E66.1.6"),sQuery(id+"F4.wireOp",EDGE,"E66.1.7"),sQuery(id+"F4.wireOp",EDGE,"E66.2.0"),sQuery(id+"F4.wireOp",EDGE,"E66.2.1"),sQuery(id+"F4.wireOp",EDGE,"E66.2.2"),sQuery(id+"F4.wireOp",EDGE,"E66.2.3"),sQuery(id+"F4.wireOp",EDGE,"E66.2.4"),sQuery(id+"F4.wireOp",EDGE,"E66.2.5"),sQuery(id+"F4.wireOp",EDGE,"E66.2.6"),sQuery(id+"F4.wireOp",EDGE,"E66.2.7"),sQuery(id+"F4.wireOp",EDGE,"E66.3.0"),sQuery(id+"F4.wireOp",EDGE,"E66.3.1"),sQuery(id+"F4.wireOp",EDGE,"E66.3.2"),sQuery(id+"F4.wireOp",EDGE,"E66.3.3"),sQuery(id+"F4.wireOp",EDGE,"E66.3.4"),sQuery(id+"F4.wireOp",EDGE,"E66.3.5"),sQuery(id+"F4.wireOp",EDGE,"E66.3.6"),sQuery(id+"F4.wireOp",EDGE,"E66.3.7"),sQuery(id+"F4.wireOp",EDGE,"E66.4.0"),sQuery(id+"F4.wireOp",EDGE,"E66.4.1"),sQuery(id+"F4.wireOp",EDGE,"E66.4.2"),sQuery(id+"F4.wireOp",EDGE,"E66.4.3"),sQuery(id+"F4.wireOp",EDGE,"E66.4.4"),sQuery(id+"F4.wireOp",EDGE,"E66.4.5"),sQuery(id+"F4.wireOp",EDGE,"E66.4.6"),sQuery(id+"F4.wireOp",EDGE,"E66.4.7"),sQuery(id+"F4.wireOp",EDGE,"E66.5.0"),sQuery(id+"F4.wireOp",EDGE,"E66.5.1"),sQuery(id+"F4.wireOp",EDGE,"E66.5.2"),sQuery(id+"F4.wireOp",EDGE,"E66.5.3"),sQuery(id+"F4.wireOp",EDGE,"E66.5.4"),sQuery(id+"F4.wireOp",EDGE,"E66.5.5"),sQuery(id+"F4.wireOp",EDGE,"E66.5.6"),sQuery(id+"F4.wireOp",EDGE,"E66.5.7"),sQuery(id+"F4.wireOp",EDGE,"E66.6.0"),sQuery(id+"F4.wireOp",EDGE,"E66.6.1"),sQuery(id+"F4.wireOp",EDGE,"E66.6.2"),sQuery(id+"F4.wireOp",EDGE,"E66.6.3"),sQuery(id+"F4.wireOp",EDGE,"E66.6.4"),sQuery(id+"F4.wireOp",EDGE,"E66.6.5"),sQuery(id+"F4.wireOp",EDGE,"E66.6.6"),sQuery(id+"F4.wireOp",EDGE,"E66.6.7"),sQuery(id+"F4.wireOp",EDGE,"E66.7.0"),sQuery(id+"F4.wireOp",EDGE,"E66.7.1"),sQuery(id+"F4.wireOp",EDGE,"E66.7.2"),sQuery(id+"F4.wireOp",EDGE,"E66.7.3"),sQuery(id+"F4.wireOp",EDGE,"E66.7.4"),sQuery(id+"F4.wireOp",EDGE,"E66.7.5"),sQuery(id+"F4.wireOp",EDGE,"E66.7.6"),sQuery(id+"F4.wireOp",EDGE,"E66.7.7"),sQuery(id+"F4.wireOp",EDGE,"E67")])]});
            hole(context, id + "F9", {"style" : HoleStyle.SIMPLE, "endStyle" : HoleEndStyle.BLIND, "standardTappedOrClearance" : lookupTablePath({ "standard" : "ANSI", "fit" : "Close", "size" : "#8", "type" : "Clearance" }), "standardBlindInLast" : lookupTablePath({ "fit" : "Close", "standard" : "ANSI", "size" : "#8", "type" : "Clearance" }), "holeDiameter" : 4.32 * mm, "holeDepth" : 5.08 * mm, "locations" : qUnion([Q0, Q1, Q2, Q3, Q4, Q5, Q6, Q7, Q8, Q9, Q10, Q11, Q12, Q13, Q14, Q15]), "scope" : qUnion([Q16])});
        }
    });
